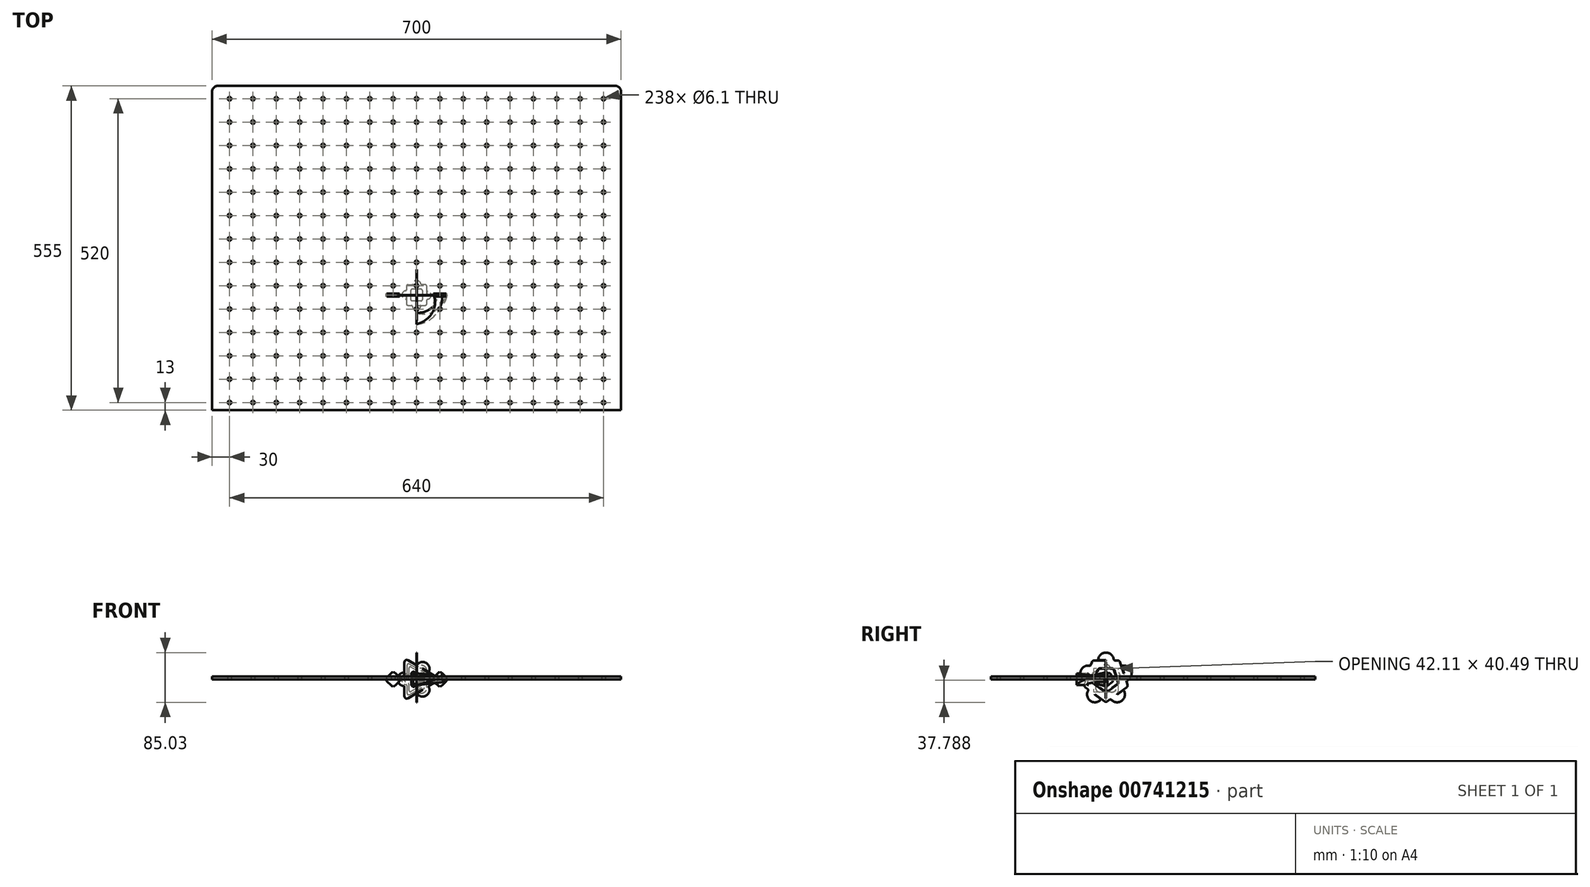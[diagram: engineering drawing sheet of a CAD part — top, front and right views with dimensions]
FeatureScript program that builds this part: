
annotation { "Feature Type Name" : "Feature", "Feature Type Description" : "" }
export const myFeature = defineFeature(function(context is Context, id is Id, definition is map)
    precondition{}
    {
        {
            var Q0;
            Q0=qCreatedBy(makeId("Top.planeOp"),FACE);
            var sketch = newSketch(context, id + "F0", { "sketchPlane" : qUnion([Q0])});
            skLineSegment(sketch, "E0.bottom", {"start": v(340, 358) * mm, "end": v(-340, 358) * mm});
            skLineSegment(sketch, "E0.top", {"start": v(340, -358) * mm, "end": v(-350, -358) * mm});
            skLineSegment(sketch, "E0.left", {"start": v(350, 348) * mm, "end": v(350, -348) * mm});
            skLineSegment(sketch, "E0.right", {"start": v(-350, 348) * mm, "end": v(-350, -358) * mm});
            skPoint(sketch, "E0.middle", {"position": v(0, 0) * mm});
            skLineSegment(sketch, "E1.0", {"start": v(324, 342) * mm, "end": v(-334, 342) * mm, "construction": true});
            skLineSegment(sketch, "E1.1", {"start": v(334, 332) * mm, "end": v(334, -342) * mm, "construction": true});
            skLineSegment(sketch, "E1.2", {"start": v(334, -342) * mm, "end": v(-334, -342) * mm, "construction": true});
            skLineSegment(sketch, "E1.3", {"start": v(-334, 342) * mm, "end": v(-334, -342) * mm, "construction": true});
            skCircle(sketch, "E2", {"center": v(-320, 336) * mm, "radius": 3.05 * mm});
            skCircle(sketch, "E3.0.1.0", {"center": v(-320, 296) * mm, "radius": 3.05 * mm});
            skCircle(sketch, "E3.1.0.0", {"center": v(-280, 336) * mm, "radius": 3.05 * mm});
            skCircle(sketch, "E3.1.1.0", {"center": v(-280, 296) * mm, "radius": 3.05 * mm});
            skCircle(sketch, "E3.2.0.0", {"center": v(-240, 336) * mm, "radius": 3.05 * mm});
            skCircle(sketch, "E3.2.1.0", {"center": v(-240, 296) * mm, "radius": 3.05 * mm});
            skCircle(sketch, "E3.3.0.0", {"center": v(-200, 336) * mm, "radius": 3.05 * mm});
            skCircle(sketch, "E3.3.1.0", {"center": v(-200, 296) * mm, "radius": 3.05 * mm});
            skCircle(sketch, "E3.4.0.0", {"center": v(-160, 336) * mm, "radius": 3.05 * mm});
            skCircle(sketch, "E3.4.1.0", {"center": v(-160, 296) * mm, "radius": 3.05 * mm});
            skCircle(sketch, "E3.5.0.0", {"center": v(-120, 336) * mm, "radius": 3.05 * mm});
            skCircle(sketch, "E3.5.1.0", {"center": v(-120, 296) * mm, "radius": 3.05 * mm});
            skCircle(sketch, "E3.6.0.0", {"center": v(-80, 336) * mm, "radius": 3.05 * mm});
            skCircle(sketch, "E3.6.1.0", {"center": v(-80, 296) * mm, "radius": 3.05 * mm});
            skCircle(sketch, "E3.7.0.0", {"center": v(-40, 336) * mm, "radius": 3.05 * mm});
            skCircle(sketch, "E3.7.1.0", {"center": v(-40, 296) * mm, "radius": 3.05 * mm});
            skCircle(sketch, "E3.8.0.0", {"center": v(0, 336) * mm, "radius": 3.05 * mm});
            skCircle(sketch, "E3.8.1.0", {"center": v(0, 296) * mm, "radius": 3.05 * mm});
            skCircle(sketch, "E3.9.0.0", {"center": v(40, 336) * mm, "radius": 3.05 * mm});
            skCircle(sketch, "E3.9.1.0", {"center": v(40, 296) * mm, "radius": 3.05 * mm});
            skCircle(sketch, "E3.10.0.0", {"center": v(80, 336) * mm, "radius": 3.05 * mm});
            skCircle(sketch, "E3.10.1.0", {"center": v(80, 296) * mm, "radius": 3.05 * mm});
            skCircle(sketch, "E3.11.0.0", {"center": v(120, 336) * mm, "radius": 3.05 * mm});
            skCircle(sketch, "E3.11.1.0", {"center": v(120, 296) * mm, "radius": 3.05 * mm});
            skCircle(sketch, "E3.12.0.0", {"center": v(160, 336) * mm, "radius": 3.05 * mm});
            skCircle(sketch, "E3.12.1.0", {"center": v(160, 296) * mm, "radius": 3.05 * mm});
            skCircle(sketch, "E3.13.0.0", {"center": v(200, 336) * mm, "radius": 3.05 * mm});
            skCircle(sketch, "E3.13.1.0", {"center": v(200, 296) * mm, "radius": 3.05 * mm});
            skLineSegment(sketch, "E3.direction1", {"start": v(-320, 336) * mm, "end": v(-280, 336) * mm, "construction": true});
            skLineSegment(sketch, "E3.direction2", {"start": v(-320, 336) * mm, "end": v(-320, 296) * mm, "construction": true});
            skCircle(sketch, "E4.0.0.2", {"center": v(-320, 256) * mm, "radius": 3.05 * mm});
            skCircle(sketch, "E4.0.0.3", {"center": v(-320, 216) * mm, "radius": 3.05 * mm});
            skCircle(sketch, "E4.0.0.4", {"center": v(-320, 176) * mm, "radius": 3.05 * mm});
            skCircle(sketch, "E4.0.0.5", {"center": v(-320, 136) * mm, "radius": 3.05 * mm});
            skCircle(sketch, "E4.0.0.6", {"center": v(-320, 96) * mm, "radius": 3.05 * mm});
            skCircle(sketch, "E4.0.0.7", {"center": v(-320, 56) * mm, "radius": 3.05 * mm});
            skCircle(sketch, "E4.0.0.8", {"center": v(-320, 16) * mm, "radius": 3.05 * mm});
            skCircle(sketch, "E4.0.0.9", {"center": v(-320, -24) * mm, "radius": 3.05 * mm});
            skCircle(sketch, "E4.0.0.10", {"center": v(-320, -64) * mm, "radius": 3.05 * mm});
            skCircle(sketch, "E4.0.0.11", {"center": v(-320, -104) * mm, "radius": 3.05 * mm});
            skCircle(sketch, "E4.0.0.12", {"center": v(-320, -144) * mm, "radius": 3.05 * mm});
            skCircle(sketch, "E4.0.0.13", {"center": v(-320, -184) * mm, "radius": 3.05 * mm});
            skCircle(sketch, "E4.0.1.2", {"center": v(-280, 256) * mm, "radius": 3.05 * mm});
            skCircle(sketch, "E4.0.1.3", {"center": v(-280, 216) * mm, "radius": 3.05 * mm});
            skCircle(sketch, "E4.0.1.4", {"center": v(-280, 176) * mm, "radius": 3.05 * mm});
            skCircle(sketch, "E4.0.1.5", {"center": v(-280, 136) * mm, "radius": 3.05 * mm});
            skCircle(sketch, "E4.0.1.6", {"center": v(-280, 96) * mm, "radius": 3.05 * mm});
            skCircle(sketch, "E4.0.1.7", {"center": v(-280, 56) * mm, "radius": 3.05 * mm});
            skCircle(sketch, "E4.0.1.8", {"center": v(-280, 16) * mm, "radius": 3.05 * mm});
            skCircle(sketch, "E4.0.1.9", {"center": v(-280, -24) * mm, "radius": 3.05 * mm});
            skCircle(sketch, "E4.0.1.10", {"center": v(-280, -64) * mm, "radius": 3.05 * mm});
            skCircle(sketch, "E4.0.1.11", {"center": v(-280, -104) * mm, "radius": 3.05 * mm});
            skCircle(sketch, "E4.0.1.12", {"center": v(-280, -144) * mm, "radius": 3.05 * mm});
            skCircle(sketch, "E4.0.1.13", {"center": v(-280, -184) * mm, "radius": 3.05 * mm});
            skCircle(sketch, "E4.0.2.2", {"center": v(-240, 256) * mm, "radius": 3.05 * mm});
            skCircle(sketch, "E4.0.2.3", {"center": v(-240, 216) * mm, "radius": 3.05 * mm});
            skCircle(sketch, "E4.0.2.4", {"center": v(-240, 176) * mm, "radius": 3.05 * mm});
            skCircle(sketch, "E4.0.2.5", {"center": v(-240, 136) * mm, "radius": 3.05 * mm});
            skCircle(sketch, "E4.0.2.6", {"center": v(-240, 96) * mm, "radius": 3.05 * mm});
            skCircle(sketch, "E4.0.2.7", {"center": v(-240, 56) * mm, "radius": 3.05 * mm});
            skCircle(sketch, "E4.0.2.8", {"center": v(-240, 16) * mm, "radius": 3.05 * mm});
            skCircle(sketch, "E4.0.2.9", {"center": v(-240, -24) * mm, "radius": 3.05 * mm});
            skCircle(sketch, "E4.0.2.10", {"center": v(-240, -64) * mm, "radius": 3.05 * mm});
            skCircle(sketch, "E4.0.2.11", {"center": v(-240, -104) * mm, "radius": 3.05 * mm});
            skCircle(sketch, "E4.0.2.12", {"center": v(-240, -144) * mm, "radius": 3.05 * mm});
            skCircle(sketch, "E4.0.2.13", {"center": v(-240, -184) * mm, "radius": 3.05 * mm});
            skCircle(sketch, "E4.0.3.2", {"center": v(-200, 256) * mm, "radius": 3.05 * mm});
            skCircle(sketch, "E4.0.3.3", {"center": v(-200, 216) * mm, "radius": 3.05 * mm});
            skCircle(sketch, "E4.0.3.4", {"center": v(-200, 176) * mm, "radius": 3.05 * mm});
            skCircle(sketch, "E4.0.3.5", {"center": v(-200, 136) * mm, "radius": 3.05 * mm});
            skCircle(sketch, "E4.0.3.6", {"center": v(-200, 96) * mm, "radius": 3.05 * mm});
            skCircle(sketch, "E4.0.3.7", {"center": v(-200, 56) * mm, "radius": 3.05 * mm});
            skCircle(sketch, "E4.0.3.8", {"center": v(-200, 16) * mm, "radius": 3.05 * mm});
            skCircle(sketch, "E4.0.3.9", {"center": v(-200, -24) * mm, "radius": 3.05 * mm});
            skCircle(sketch, "E4.0.3.10", {"center": v(-200, -64) * mm, "radius": 3.05 * mm});
            skCircle(sketch, "E4.0.3.11", {"center": v(-200, -104) * mm, "radius": 3.05 * mm});
            skCircle(sketch, "E4.0.3.12", {"center": v(-200, -144) * mm, "radius": 3.05 * mm});
            skCircle(sketch, "E4.0.3.13", {"center": v(-200, -184) * mm, "radius": 3.05 * mm});
            skCircle(sketch, "E4.0.4.2", {"center": v(-160, 256) * mm, "radius": 3.05 * mm});
            skCircle(sketch, "E4.0.4.3", {"center": v(-160, 216) * mm, "radius": 3.05 * mm});
            skCircle(sketch, "E4.0.4.4", {"center": v(-160, 176) * mm, "radius": 3.05 * mm});
            skCircle(sketch, "E4.0.4.5", {"center": v(-160, 136) * mm, "radius": 3.05 * mm});
            skCircle(sketch, "E4.0.4.6", {"center": v(-160, 96) * mm, "radius": 3.05 * mm});
            skCircle(sketch, "E4.0.4.7", {"center": v(-160, 56) * mm, "radius": 3.05 * mm});
            skCircle(sketch, "E4.0.4.8", {"center": v(-160, 16) * mm, "radius": 3.05 * mm});
            skCircle(sketch, "E4.0.4.9", {"center": v(-160, -24) * mm, "radius": 3.05 * mm});
            skCircle(sketch, "E4.0.4.10", {"center": v(-160, -64) * mm, "radius": 3.05 * mm});
            skCircle(sketch, "E4.0.4.11", {"center": v(-160, -104) * mm, "radius": 3.05 * mm});
            skCircle(sketch, "E4.0.4.12", {"center": v(-160, -144) * mm, "radius": 3.05 * mm});
            skCircle(sketch, "E4.0.4.13", {"center": v(-160, -184) * mm, "radius": 3.05 * mm});
            skCircle(sketch, "E4.0.5.2", {"center": v(-120, 256) * mm, "radius": 3.05 * mm});
            skCircle(sketch, "E4.0.5.3", {"center": v(-120, 216) * mm, "radius": 3.05 * mm});
            skCircle(sketch, "E4.0.5.4", {"center": v(-120, 176) * mm, "radius": 3.05 * mm});
            skCircle(sketch, "E4.0.5.5", {"center": v(-120, 136) * mm, "radius": 3.05 * mm});
            skCircle(sketch, "E4.0.5.6", {"center": v(-120, 96) * mm, "radius": 3.05 * mm});
            skCircle(sketch, "E4.0.5.7", {"center": v(-120, 56) * mm, "radius": 3.05 * mm});
            skCircle(sketch, "E4.0.5.8", {"center": v(-120, 16) * mm, "radius": 3.05 * mm});
            skCircle(sketch, "E4.0.5.9", {"center": v(-120, -24) * mm, "radius": 3.05 * mm});
            skCircle(sketch, "E4.0.5.10", {"center": v(-120, -64) * mm, "radius": 3.05 * mm});
            skCircle(sketch, "E4.0.5.11", {"center": v(-120, -104) * mm, "radius": 3.05 * mm});
            skCircle(sketch, "E4.0.5.12", {"center": v(-120, -144) * mm, "radius": 3.05 * mm});
            skCircle(sketch, "E4.0.5.13", {"center": v(-120, -184) * mm, "radius": 3.05 * mm});
            skCircle(sketch, "E4.0.6.2", {"center": v(-80, 256) * mm, "radius": 3.05 * mm});
            skCircle(sketch, "E4.0.6.3", {"center": v(-80, 216) * mm, "radius": 3.05 * mm});
            skCircle(sketch, "E4.0.6.4", {"center": v(-80, 176) * mm, "radius": 3.05 * mm});
            skCircle(sketch, "E4.0.6.5", {"center": v(-80, 136) * mm, "radius": 3.05 * mm});
            skCircle(sketch, "E4.0.6.6", {"center": v(-80, 96) * mm, "radius": 3.05 * mm});
            skCircle(sketch, "E4.0.6.7", {"center": v(-80, 56) * mm, "radius": 3.05 * mm});
            skCircle(sketch, "E4.0.6.8", {"center": v(-80, 16) * mm, "radius": 3.05 * mm});
            skCircle(sketch, "E4.0.6.9", {"center": v(-80, -24) * mm, "radius": 3.05 * mm});
            skCircle(sketch, "E4.0.6.10", {"center": v(-80, -64) * mm, "radius": 3.05 * mm});
            skCircle(sketch, "E4.0.6.11", {"center": v(-80, -104) * mm, "radius": 3.05 * mm});
            skCircle(sketch, "E4.0.6.12", {"center": v(-80, -144) * mm, "radius": 3.05 * mm});
            skCircle(sketch, "E4.0.6.13", {"center": v(-80, -184) * mm, "radius": 3.05 * mm});
            skCircle(sketch, "E4.0.7.2", {"center": v(-40, 256) * mm, "radius": 3.05 * mm});
            skCircle(sketch, "E4.0.7.3", {"center": v(-40, 216) * mm, "radius": 3.05 * mm});
            skCircle(sketch, "E4.0.7.4", {"center": v(-40, 176) * mm, "radius": 3.05 * mm});
            skCircle(sketch, "E4.0.7.5", {"center": v(-40, 136) * mm, "radius": 3.05 * mm});
            skCircle(sketch, "E4.0.7.6", {"center": v(-40, 96) * mm, "radius": 3.05 * mm});
            skCircle(sketch, "E4.0.7.7", {"center": v(-40, 56) * mm, "radius": 3.05 * mm});
            skCircle(sketch, "E4.0.7.8", {"center": v(-40, 16) * mm, "radius": 3.05 * mm});
            skCircle(sketch, "E4.0.7.9", {"center": v(-40, -24) * mm, "radius": 3.05 * mm});
            skCircle(sketch, "E4.0.7.10", {"center": v(-40, -64) * mm, "radius": 3.05 * mm});
            skCircle(sketch, "E4.0.7.11", {"center": v(-40, -104) * mm, "radius": 3.05 * mm});
            skCircle(sketch, "E4.0.7.12", {"center": v(-40, -144) * mm, "radius": 3.05 * mm});
            skCircle(sketch, "E4.0.7.13", {"center": v(-40, -184) * mm, "radius": 3.05 * mm});
            skCircle(sketch, "E4.0.8.2", {"center": v(0, 256) * mm, "radius": 3.05 * mm});
            skCircle(sketch, "E4.0.8.3", {"center": v(0, 216) * mm, "radius": 3.05 * mm});
            skCircle(sketch, "E4.0.8.4", {"center": v(0, 176) * mm, "radius": 3.05 * mm});
            skCircle(sketch, "E4.0.8.5", {"center": v(0, 136) * mm, "radius": 3.05 * mm});
            skCircle(sketch, "E4.0.8.6", {"center": v(0, 96) * mm, "radius": 3.05 * mm});
            skCircle(sketch, "E4.0.8.7", {"center": v(0, 56) * mm, "radius": 3.05 * mm});
            skCircle(sketch, "E4.0.8.8", {"center": v(0, 16) * mm, "radius": 3.05 * mm});
            skCircle(sketch, "E4.0.8.9", {"center": v(0, -24) * mm, "radius": 3.05 * mm});
            skCircle(sketch, "E4.0.8.10", {"center": v(0, -64) * mm, "radius": 3.05 * mm});
            skCircle(sketch, "E4.0.8.11", {"center": v(0, -104) * mm, "radius": 3.05 * mm});
            skCircle(sketch, "E4.0.8.12", {"center": v(0, -144) * mm, "radius": 3.05 * mm});
            skCircle(sketch, "E4.0.8.13", {"center": v(0, -184) * mm, "radius": 3.05 * mm});
            skCircle(sketch, "E4.0.9.2", {"center": v(40, 256) * mm, "radius": 3.05 * mm});
            skCircle(sketch, "E4.0.9.3", {"center": v(40, 216) * mm, "radius": 3.05 * mm});
            skCircle(sketch, "E4.0.9.4", {"center": v(40, 176) * mm, "radius": 3.05 * mm});
            skCircle(sketch, "E4.0.9.5", {"center": v(40, 136) * mm, "radius": 3.05 * mm});
            skCircle(sketch, "E4.0.9.6", {"center": v(40, 96) * mm, "radius": 3.05 * mm});
            skCircle(sketch, "E4.0.9.7", {"center": v(40, 56) * mm, "radius": 3.05 * mm});
            skCircle(sketch, "E4.0.9.8", {"center": v(40, 16) * mm, "radius": 3.05 * mm});
            skCircle(sketch, "E4.0.9.9", {"center": v(40, -24) * mm, "radius": 3.05 * mm});
            skCircle(sketch, "E4.0.9.10", {"center": v(40, -64) * mm, "radius": 3.05 * mm});
            skCircle(sketch, "E4.0.9.11", {"center": v(40, -104) * mm, "radius": 3.05 * mm});
            skCircle(sketch, "E4.0.9.12", {"center": v(40, -144) * mm, "radius": 3.05 * mm});
            skCircle(sketch, "E4.0.9.13", {"center": v(40, -184) * mm, "radius": 3.05 * mm});
            skCircle(sketch, "E4.0.10.2", {"center": v(80, 256) * mm, "radius": 3.05 * mm});
            skCircle(sketch, "E4.0.10.3", {"center": v(80, 216) * mm, "radius": 3.05 * mm});
            skCircle(sketch, "E4.0.10.4", {"center": v(80, 176) * mm, "radius": 3.05 * mm});
            skCircle(sketch, "E4.0.10.5", {"center": v(80, 136) * mm, "radius": 3.05 * mm});
            skCircle(sketch, "E4.0.10.6", {"center": v(80, 96) * mm, "radius": 3.05 * mm});
            skCircle(sketch, "E4.0.10.7", {"center": v(80, 56) * mm, "radius": 3.05 * mm});
            skCircle(sketch, "E4.0.10.8", {"center": v(80, 16) * mm, "radius": 3.05 * mm});
            skCircle(sketch, "E4.0.10.9", {"center": v(80, -24) * mm, "radius": 3.05 * mm});
            skCircle(sketch, "E4.0.10.10", {"center": v(80, -64) * mm, "radius": 3.05 * mm});
            skCircle(sketch, "E4.0.10.11", {"center": v(80, -104) * mm, "radius": 3.05 * mm});
            skCircle(sketch, "E4.0.10.12", {"center": v(80, -144) * mm, "radius": 3.05 * mm});
            skCircle(sketch, "E4.0.10.13", {"center": v(80, -184) * mm, "radius": 3.05 * mm});
            skCircle(sketch, "E4.0.11.2", {"center": v(120, 256) * mm, "radius": 3.05 * mm});
            skCircle(sketch, "E4.0.11.3", {"center": v(120, 216) * mm, "radius": 3.05 * mm});
            skCircle(sketch, "E4.0.11.4", {"center": v(120, 176) * mm, "radius": 3.05 * mm});
            skCircle(sketch, "E4.0.11.5", {"center": v(120, 136) * mm, "radius": 3.05 * mm});
            skCircle(sketch, "E4.0.11.6", {"center": v(120, 96) * mm, "radius": 3.05 * mm});
            skCircle(sketch, "E4.0.11.7", {"center": v(120, 56) * mm, "radius": 3.05 * mm});
            skCircle(sketch, "E4.0.11.8", {"center": v(120, 16) * mm, "radius": 3.05 * mm});
            skCircle(sketch, "E4.0.11.9", {"center": v(120, -24) * mm, "radius": 3.05 * mm});
            skCircle(sketch, "E4.0.11.10", {"center": v(120, -64) * mm, "radius": 3.05 * mm});
            skCircle(sketch, "E4.0.11.11", {"center": v(120, -104) * mm, "radius": 3.05 * mm});
            skCircle(sketch, "E4.0.11.12", {"center": v(120, -144) * mm, "radius": 3.05 * mm});
            skCircle(sketch, "E4.0.11.13", {"center": v(120, -184) * mm, "radius": 3.05 * mm});
            skCircle(sketch, "E4.0.12.2", {"center": v(160, 256) * mm, "radius": 3.05 * mm});
            skCircle(sketch, "E4.0.12.3", {"center": v(160, 216) * mm, "radius": 3.05 * mm});
            skCircle(sketch, "E4.0.12.4", {"center": v(160, 176) * mm, "radius": 3.05 * mm});
            skCircle(sketch, "E4.0.12.5", {"center": v(160, 136) * mm, "radius": 3.05 * mm});
            skCircle(sketch, "E4.0.12.6", {"center": v(160, 96) * mm, "radius": 3.05 * mm});
            skCircle(sketch, "E4.0.12.7", {"center": v(160, 56) * mm, "radius": 3.05 * mm});
            skCircle(sketch, "E4.0.12.8", {"center": v(160, 16) * mm, "radius": 3.05 * mm});
            skCircle(sketch, "E4.0.12.9", {"center": v(160, -24) * mm, "radius": 3.05 * mm});
            skCircle(sketch, "E4.0.12.10", {"center": v(160, -64) * mm, "radius": 3.05 * mm});
            skCircle(sketch, "E4.0.12.11", {"center": v(160, -104) * mm, "radius": 3.05 * mm});
            skCircle(sketch, "E4.0.12.12", {"center": v(160, -144) * mm, "radius": 3.05 * mm});
            skCircle(sketch, "E4.0.12.13", {"center": v(160, -184) * mm, "radius": 3.05 * mm});
            skCircle(sketch, "E4.0.13.2", {"center": v(200, 256) * mm, "radius": 3.05 * mm});
            skCircle(sketch, "E4.0.13.3", {"center": v(200, 216) * mm, "radius": 3.05 * mm});
            skCircle(sketch, "E4.0.13.4", {"center": v(200, 176) * mm, "radius": 3.05 * mm});
            skCircle(sketch, "E4.0.13.5", {"center": v(200, 136) * mm, "radius": 3.05 * mm});
            skCircle(sketch, "E4.0.13.6", {"center": v(200, 96) * mm, "radius": 3.05 * mm});
            skCircle(sketch, "E4.0.13.7", {"center": v(200, 56) * mm, "radius": 3.05 * mm});
            skCircle(sketch, "E4.0.13.8", {"center": v(200, 16) * mm, "radius": 3.05 * mm});
            skCircle(sketch, "E4.0.13.9", {"center": v(200, -24) * mm, "radius": 3.05 * mm});
            skCircle(sketch, "E4.0.13.10", {"center": v(200, -64) * mm, "radius": 3.05 * mm});
            skCircle(sketch, "E4.0.13.11", {"center": v(200, -104) * mm, "radius": 3.05 * mm});
            skCircle(sketch, "E4.0.13.12", {"center": v(200, -144) * mm, "radius": 3.05 * mm});
            skCircle(sketch, "E4.0.13.13", {"center": v(200, -184) * mm, "radius": 3.05 * mm});
            skLineSegment(sketch, "E5", {"start": v(0, 358) * mm, "end": v(0, -358) * mm});
            skCircle(sketch, "E6.0.14.0", {"center": v(240, 336) * mm, "radius": 3.05 * mm});
            skCircle(sketch, "E6.0.14.1", {"center": v(240, 296) * mm, "radius": 3.05 * mm});
            skCircle(sketch, "E6.0.14.2", {"center": v(240, 256) * mm, "radius": 3.05 * mm});
            skCircle(sketch, "E6.0.14.3", {"center": v(240, 216) * mm, "radius": 3.05 * mm});
            skCircle(sketch, "E6.0.14.4", {"center": v(240, 176) * mm, "radius": 3.05 * mm});
            skCircle(sketch, "E6.0.14.5", {"center": v(240, 136) * mm, "radius": 3.05 * mm});
            skCircle(sketch, "E6.0.14.6", {"center": v(240, 96) * mm, "radius": 3.05 * mm});
            skCircle(sketch, "E6.0.14.7", {"center": v(240, 56) * mm, "radius": 3.05 * mm});
            skCircle(sketch, "E6.0.14.8", {"center": v(240, 16) * mm, "radius": 3.05 * mm});
            skCircle(sketch, "E6.0.14.9", {"center": v(240, -24) * mm, "radius": 3.05 * mm});
            skCircle(sketch, "E6.0.14.10", {"center": v(240, -64) * mm, "radius": 3.05 * mm});
            skCircle(sketch, "E6.0.14.11", {"center": v(240, -104) * mm, "radius": 3.05 * mm});
            skCircle(sketch, "E6.0.14.12", {"center": v(240, -144) * mm, "radius": 3.05 * mm});
            skCircle(sketch, "E6.0.14.13", {"center": v(240, -184) * mm, "radius": 3.05 * mm});
            skCircle(sketch, "E6.0.15.0", {"center": v(280, 336) * mm, "radius": 3.05 * mm});
            skCircle(sketch, "E6.0.15.1", {"center": v(280, 296) * mm, "radius": 3.05 * mm});
            skCircle(sketch, "E6.0.15.2", {"center": v(280, 256) * mm, "radius": 3.05 * mm});
            skCircle(sketch, "E6.0.15.3", {"center": v(280, 216) * mm, "radius": 3.05 * mm});
            skCircle(sketch, "E6.0.15.4", {"center": v(280, 176) * mm, "radius": 3.05 * mm});
            skCircle(sketch, "E6.0.15.5", {"center": v(280, 136) * mm, "radius": 3.05 * mm});
            skCircle(sketch, "E6.0.15.6", {"center": v(280, 96) * mm, "radius": 3.05 * mm});
            skCircle(sketch, "E6.0.15.7", {"center": v(280, 56) * mm, "radius": 3.05 * mm});
            skCircle(sketch, "E6.0.15.8", {"center": v(280, 16) * mm, "radius": 3.05 * mm});
            skCircle(sketch, "E6.0.15.9", {"center": v(280, -24) * mm, "radius": 3.05 * mm});
            skCircle(sketch, "E6.0.15.10", {"center": v(280, -64) * mm, "radius": 3.05 * mm});
            skCircle(sketch, "E6.0.15.11", {"center": v(280, -104) * mm, "radius": 3.05 * mm});
            skCircle(sketch, "E6.0.15.12", {"center": v(280, -144) * mm, "radius": 3.05 * mm});
            skCircle(sketch, "E6.0.15.13", {"center": v(280, -184) * mm, "radius": 3.05 * mm});
            skCircle(sketch, "E6.0.16.0", {"center": v(320, 336) * mm, "radius": 3.05 * mm});
            skCircle(sketch, "E6.0.16.1", {"center": v(320, 296) * mm, "radius": 3.05 * mm});
            skCircle(sketch, "E6.0.16.2", {"center": v(320, 256) * mm, "radius": 3.05 * mm});
            skCircle(sketch, "E6.0.16.3", {"center": v(320, 216) * mm, "radius": 3.05 * mm});
            skCircle(sketch, "E6.0.16.4", {"center": v(320, 176) * mm, "radius": 3.05 * mm});
            skCircle(sketch, "E6.0.16.5", {"center": v(320, 136) * mm, "radius": 3.05 * mm});
            skCircle(sketch, "E6.0.16.6", {"center": v(320, 96) * mm, "radius": 3.05 * mm});
            skCircle(sketch, "E6.0.16.7", {"center": v(320, 56) * mm, "radius": 3.05 * mm});
            skCircle(sketch, "E6.0.16.8", {"center": v(320, 16) * mm, "radius": 3.05 * mm});
            skCircle(sketch, "E6.0.16.9", {"center": v(320, -24) * mm, "radius": 3.05 * mm});
            skCircle(sketch, "E6.0.16.10", {"center": v(320, -64) * mm, "radius": 3.05 * mm});
            skCircle(sketch, "E6.0.16.11", {"center": v(320, -104) * mm, "radius": 3.05 * mm});
            skCircle(sketch, "E6.0.16.12", {"center": v(320, -144) * mm, "radius": 3.05 * mm});
            skCircle(sketch, "E6.0.16.13", {"center": v(320, -184) * mm, "radius": 3.05 * mm});
            skCircle(sketch, "E7.0.0.14", {"center": v(-320, -224) * mm, "radius": 3.05 * mm});
            skCircle(sketch, "E7.0.0.15", {"center": v(-320, -264) * mm, "radius": 3.05 * mm});
            skCircle(sketch, "E7.0.0.16", {"center": v(-320, -304) * mm, "radius": 3.05 * mm});
            skCircle(sketch, "E7.0.1.14", {"center": v(-280, -224) * mm, "radius": 3.05 * mm});
            skCircle(sketch, "E7.0.1.15", {"center": v(-280, -264) * mm, "radius": 3.05 * mm});
            skCircle(sketch, "E7.0.1.16", {"center": v(-280, -304) * mm, "radius": 3.05 * mm});
            skCircle(sketch, "E7.0.2.14", {"center": v(-240, -224) * mm, "radius": 3.05 * mm});
            skCircle(sketch, "E7.0.2.15", {"center": v(-240, -264) * mm, "radius": 3.05 * mm});
            skCircle(sketch, "E7.0.2.16", {"center": v(-240, -304) * mm, "radius": 3.05 * mm});
            skCircle(sketch, "E7.0.3.14", {"center": v(-200, -224) * mm, "radius": 3.05 * mm});
            skCircle(sketch, "E7.0.3.15", {"center": v(-200, -264) * mm, "radius": 3.05 * mm});
            skCircle(sketch, "E7.0.3.16", {"center": v(-200, -304) * mm, "radius": 3.05 * mm});
            skCircle(sketch, "E7.0.4.14", {"center": v(-160, -224) * mm, "radius": 3.05 * mm});
            skCircle(sketch, "E7.0.4.15", {"center": v(-160, -264) * mm, "radius": 3.05 * mm});
            skCircle(sketch, "E7.0.4.16", {"center": v(-160, -304) * mm, "radius": 3.05 * mm});
            skCircle(sketch, "E7.0.5.14", {"center": v(-120, -224) * mm, "radius": 3.05 * mm});
            skCircle(sketch, "E7.0.5.15", {"center": v(-120, -264) * mm, "radius": 3.05 * mm});
            skCircle(sketch, "E7.0.5.16", {"center": v(-120, -304) * mm, "radius": 3.05 * mm});
            skCircle(sketch, "E7.0.6.14", {"center": v(-80, -224) * mm, "radius": 3.05 * mm});
            skCircle(sketch, "E7.0.6.15", {"center": v(-80, -264) * mm, "radius": 3.05 * mm});
            skCircle(sketch, "E7.0.6.16", {"center": v(-80, -304) * mm, "radius": 3.05 * mm});
            skCircle(sketch, "E7.0.7.14", {"center": v(-40, -224) * mm, "radius": 3.05 * mm});
            skCircle(sketch, "E7.0.7.15", {"center": v(-40, -264) * mm, "radius": 3.05 * mm});
            skCircle(sketch, "E7.0.7.16", {"center": v(-40, -304) * mm, "radius": 3.05 * mm});
            skCircle(sketch, "E7.0.8.14", {"center": v(0, -224) * mm, "radius": 3.05 * mm});
            skCircle(sketch, "E7.0.8.15", {"center": v(0, -264) * mm, "radius": 3.05 * mm});
            skCircle(sketch, "E7.0.8.16", {"center": v(0, -304) * mm, "radius": 3.05 * mm});
            skCircle(sketch, "E7.0.9.14", {"center": v(40, -224) * mm, "radius": 3.05 * mm});
            skCircle(sketch, "E7.0.9.15", {"center": v(40, -264) * mm, "radius": 3.05 * mm});
            skCircle(sketch, "E7.0.9.16", {"center": v(40, -304) * mm, "radius": 3.05 * mm});
            skCircle(sketch, "E7.0.10.14", {"center": v(80, -224) * mm, "radius": 3.05 * mm});
            skCircle(sketch, "E7.0.10.15", {"center": v(80, -264) * mm, "radius": 3.05 * mm});
            skCircle(sketch, "E7.0.10.16", {"center": v(80, -304) * mm, "radius": 3.05 * mm});
            skCircle(sketch, "E7.0.11.14", {"center": v(120, -224) * mm, "radius": 3.05 * mm});
            skCircle(sketch, "E7.0.11.15", {"center": v(120, -264) * mm, "radius": 3.05 * mm});
            skCircle(sketch, "E7.0.11.16", {"center": v(120, -304) * mm, "radius": 3.05 * mm});
            skCircle(sketch, "E7.0.12.14", {"center": v(160, -224) * mm, "radius": 3.05 * mm});
            skCircle(sketch, "E7.0.12.15", {"center": v(160, -264) * mm, "radius": 3.05 * mm});
            skCircle(sketch, "E7.0.12.16", {"center": v(160, -304) * mm, "radius": 3.05 * mm});
            skCircle(sketch, "E7.0.13.14", {"center": v(200, -224) * mm, "radius": 3.05 * mm});
            skCircle(sketch, "E7.0.13.15", {"center": v(200, -264) * mm, "radius": 3.05 * mm});
            skCircle(sketch, "E7.0.13.16", {"center": v(200, -304) * mm, "radius": 3.05 * mm});
            skCircle(sketch, "E7.0.14.14", {"center": v(240, -224) * mm, "radius": 3.05 * mm});
            skCircle(sketch, "E7.0.14.15", {"center": v(240, -264) * mm, "radius": 3.05 * mm});
            skCircle(sketch, "E7.0.14.16", {"center": v(240, -304) * mm, "radius": 3.05 * mm});
            skCircle(sketch, "E7.0.15.14", {"center": v(280, -224) * mm, "radius": 3.05 * mm});
            skCircle(sketch, "E7.0.15.15", {"center": v(280, -264) * mm, "radius": 3.05 * mm});
            skCircle(sketch, "E7.0.15.16", {"center": v(280, -304) * mm, "radius": 3.05 * mm});
            skCircle(sketch, "E7.0.16.14", {"center": v(320, -224) * mm, "radius": 3.05 * mm});
            skCircle(sketch, "E7.0.16.15", {"center": v(320, -264) * mm, "radius": 3.05 * mm});
            skCircle(sketch, "E7.0.16.16", {"center": v(320, -304) * mm, "radius": 3.05 * mm});
            skPoint(sketch, "E8.visualSharp", {"position": v(334, 342) * mm});
            skPoint(sketch, "E9.visualSharp", {"position": v(350, -358) * mm});
            skArc(sketch, "E9.filletArc", {"start": v(340, -358) * mm, "mid": v(347.07, -355.07) * mm, "end": v(350, -348) * mm});
            skPoint(sketch, "E10.visualSharp", {"position": v(350, 358) * mm});
            skArc(sketch, "E10.filletArc", {"start": v(350, 348) * mm, "mid": v(347.07, 355.07) * mm, "end": v(340, 358) * mm});
            skLineSegment(sketch, "E11", {"start": v(-350, -197) * mm, "end": v(350, -197) * mm});
            skPoint(sketch, "E12.visualSharp", {"position": v(-350, 358) * mm});
            skArc(sketch, "E12.filletArc", {"start": v(-340, 358) * mm, "mid": v(-347.07, 355.07) * mm, "end": v(-350, 348) * mm});
            skSolve(sketch);
        }
        {
            var Q0;
            Q0=makeQuery(id+"F0.imprint","IMPRINT",FACE,{"disambiguationData":[TD([[makeQuery(id+"F0.imprint","IMPRINT",EDGE,{"derivedFrom":sQuery(id+"F0.wireOp",EDGE,"E2")}),-1.0]])]});
            var Q1;
            Q1=makeQuery(id+"F0.imprint","IMPRINT",FACE,{"disambiguationData":[TD([[makeQuery(id+"F0.imprint","IMPRINT",EDGE,{"derivedFrom":sQuery(id+"F0.wireOp",EDGE,"E3.9.0.0")}),-1.0]])]});
            extrude(context, id + "F1", {"entities" : qUnion([Q0, Q1]), "depth" : 5 * mm, "offsetDistance" : 25 * mm});
        }
        {
            var Q0;
            Q0=qCreatedBy(makeId("Top.planeOp"),FACE);
            var sketch = newSketch(context, id + "F2", { "sketchPlane" : qUnion([Q0])});
            skLineSegment(sketch, "E13.bottom", {"start": v(15, 20) * mm, "end": v(-15, 20) * mm});
            skLineSegment(sketch, "E13.top", {"start": v(15, -20) * mm, "end": v(-15, -20) * mm});
            skLineSegment(sketch, "E13.left", {"start": v(20, 15) * mm, "end": v(20, -15) * mm});
            skLineSegment(sketch, "E13.right", {"start": v(-20, 15) * mm, "end": v(-20, -15) * mm});
            skPoint(sketch, "E13.middle", {"position": v(0, 0) * mm});
            skLineSegment(sketch, "E14.2", {"start": v(-35, 30) * mm, "end": v(-35, 15) * mm});
            skArc(sketch, "E15", {"start": v(-35, 15) * mm, "mid": v(-49.9, 1.74) * mm, "end": v(-38.46, -14.6) * mm});
            skLineSegment(sketch, "E16.trimOffspring", {"start": v(-35, -15) * mm, "end": v(-35, -30) * mm});
            skLineSegment(sketch, "E17.left", {"start": v(-35, 0) * mm, "end": v(-35, -15) * mm});
            skLineSegment(sketch, "E17.right", {"start": v(-36, 0) * mm, "end": v(-36, -12.65) * mm});
            skPoint(sketch, "E18.visualSharp", {"position": v(-35, 35) * mm});
            skArc(sketch, "E18.filletArc", {"start": v(-30, 35) * mm, "mid": v(-33.54, 33.54) * mm, "end": v(-35, 30) * mm});
            skPoint(sketch, "E19.visualSharp", {"position": v(-20, 20) * mm});
            skArc(sketch, "E19.filletArc", {"start": v(-15, 20) * mm, "mid": v(-18.54, 18.54) * mm, "end": v(-20, 15) * mm});
            skPoint(sketch, "E20.visualSharp", {"position": v(20, 20) * mm});
            skArc(sketch, "E20.filletArc", {"start": v(20, 15) * mm, "mid": v(18.54, 18.54) * mm, "end": v(15, 20) * mm});
            skPoint(sketch, "E21.visualSharp", {"position": v(35, 35) * mm});
            skArc(sketch, "E21.filletArc", {"start": v(35, 30) * mm, "mid": v(33.54, 33.54) * mm, "end": v(30, 35) * mm});
            skPoint(sketch, "E22.visualSharp", {"position": v(20, -20) * mm});
            skArc(sketch, "E22.filletArc", {"start": v(15, -20) * mm, "mid": v(18.54, -18.54) * mm, "end": v(20, -15) * mm});
            skPoint(sketch, "E23.visualSharp", {"position": v(-20, -20) * mm});
            skArc(sketch, "E23.filletArc", {"start": v(-20, -15) * mm, "mid": v(-18.54, -18.54) * mm, "end": v(-15, -20) * mm});
            skPoint(sketch, "E24.visualSharp", {"position": v(-35, -35) * mm});
            skArc(sketch, "E24.filletArc", {"start": v(-35, -30) * mm, "mid": v(-33.54, -33.54) * mm, "end": v(-30, -35) * mm});
            skPoint(sketch, "E25.visualSharp", {"position": v(35, -35) * mm});
            skArc(sketch, "E25.filletArc", {"start": v(30, -35) * mm, "mid": v(33.54, -33.54) * mm, "end": v(35, -30) * mm});
            skLineSegment(sketch, "E26.1.0", {"start": v(-30, -35) * mm, "end": v(-15, -35) * mm});
            skArc(sketch, "E26.1.1", {"start": v(-15, -35) * mm, "mid": v(-1.74, -49.9) * mm, "end": v(14.6, -38.46) * mm});
            skLineSegment(sketch, "E26.1.2", {"start": v(0, -36) * mm, "end": v(12.65, -36) * mm});
            skLineSegment(sketch, "E26.1.4", {"start": v(0, -35) * mm, "end": v(0, -36) * mm});
            skLineSegment(sketch, "E26.2.0", {"start": v(35, -30) * mm, "end": v(35, -15) * mm});
            skArc(sketch, "E26.2.1", {"start": v(35, -15) * mm, "mid": v(49.9, -1.74) * mm, "end": v(38.46, 14.6) * mm});
            skLineSegment(sketch, "E26.2.2", {"start": v(36, 0) * mm, "end": v(36, 12.65) * mm});
            skLineSegment(sketch, "E26.2.3", {"start": v(35, 0) * mm, "end": v(35, 15) * mm});
            skLineSegment(sketch, "E26.2.4", {"start": v(35, 0) * mm, "end": v(36, 0) * mm});
            skLineSegment(sketch, "E26.2.5", {"start": v(35, 15) * mm, "end": v(35, 30) * mm});
            skLineSegment(sketch, "E26.3.0", {"start": v(30, 35) * mm, "end": v(15, 35) * mm});
            skArc(sketch, "E26.3.1", {"start": v(15, 35) * mm, "mid": v(1.74, 49.9) * mm, "end": v(-14.6, 38.46) * mm});
            skLineSegment(sketch, "E26.3.2", {"start": v(0, 36) * mm, "end": v(-12.65, 36) * mm});
            skLineSegment(sketch, "E26.3.4", {"start": v(0, 35) * mm, "end": v(0, 36) * mm});
            skLineSegment(sketch, "E27", {"start": v(-30, 35) * mm, "end": v(0, 35) * mm});
            skLineSegment(sketch, "E28", {"start": v(0, -35) * mm, "end": v(30, -35) * mm});
            skPoint(sketch, "E29.visualSharp", {"position": v(-14.97, 36) * mm});
            skArc(sketch, "E29.filletArc", {"start": v(-14.6, 38.46) * mm, "mid": v(-14.22, 36.76) * mm, "end": v(-12.65, 36) * mm});
            skPoint(sketch, "E30.visualSharp", {"position": v(36, 14.97) * mm});
            skArc(sketch, "E30.filletArc", {"start": v(38.46, 14.6) * mm, "mid": v(36.76, 14.22) * mm, "end": v(36, 12.65) * mm});
            skPoint(sketch, "E31.visualSharp", {"position": v(14.97, -36) * mm});
            skArc(sketch, "E31.filletArc", {"start": v(14.6, -38.46) * mm, "mid": v(14.22, -36.76) * mm, "end": v(12.65, -36) * mm});
            skPoint(sketch, "E32.visualSharp", {"position": v(-36, -14.97) * mm});
            skArc(sketch, "E32.filletArc", {"start": v(-38.46, -14.6) * mm, "mid": v(-36.76, -14.22) * mm, "end": v(-36, -12.65) * mm});
            skLineSegment(sketch, "E33", {"start": v(-36, 0) * mm, "end": v(-35, 0) * mm});
            skSolve(sketch);
        }
        {
            var Q0;
            Q0=makeQuery(id+"F2.imprint","IMPRINT",FACE,{"disambiguationData":[TD([[makeQuery(id+"F2.imprint","IMPRINT",EDGE,{"derivedFrom":sQuery(id+"F2.wireOp",EDGE,"E13.bottom")}),-1.0]])]});
            extrude(context, id + "F3", {"entities" : qUnion([Q0]), "depth" : 0.5 * mm, "offsetDistance" : 25 * mm});
        }
        {
            var Q0;
            Q0=qCreatedBy(makeId("Front.planeOp"),FACE);
            var sketch = newSketch(context, id + "F4", { "sketchPlane" : qUnion([Q0])});
            skLineSegment(sketch, "E34.0", {"start": v(-11.55, -11.34) * mm, "end": v(-11.55, 11.34) * mm});
            skLineSegment(sketch, "E34.1", {"start": v(-4.05, 15.67) * mm, "end": v(15.6, 4.33) * mm});
            skLineSegment(sketch, "E34.2", {"start": v(15.6, -4.33) * mm, "end": v(-4.05, -15.67) * mm});
            skPoint(sketch, "E34.0.midPoint", {"position": v(-11.55, 0) * mm});
            skPoint(sketch, "E35.visualSharp", {"position": v(-26.55, 45.98) * mm});
            skArc(sketch, "E35.filletArc", {"start": v(-19.05, 41.65) * mm, "mid": v(-24.05, 41.65) * mm, "end": v(-26.55, 37.32) * mm});
            skPoint(sketch, "E36.visualSharp", {"position": v(-11.55, 20) * mm});
            skArc(sketch, "E36.filletArc", {"start": v(-4.05, 15.67) * mm, "mid": v(-9.05, 15.67) * mm, "end": v(-11.55, 11.34) * mm});
            skPoint(sketch, "E37.visualSharp", {"position": v(-11.55, -20) * mm});
            skArc(sketch, "E37.filletArc", {"start": v(-11.55, -11.34) * mm, "mid": v(-9.05, -15.67) * mm, "end": v(-4.05, -15.67) * mm});
            skPoint(sketch, "E38.visualSharp", {"position": v(-26.55, -45.98) * mm});
            skArc(sketch, "E38.filletArc", {"start": v(-26.55, -37.32) * mm, "mid": v(-24.05, -41.65) * mm, "end": v(-19.05, -41.65) * mm});
            skPoint(sketch, "E39.visualSharp", {"position": v(23.1, 0) * mm});
            skArc(sketch, "E39.filletArc", {"start": v(15.6, -4.33) * mm, "mid": v(18.1, 0) * mm, "end": v(15.6, 4.33) * mm});
            skPoint(sketch, "E40.visualSharp", {"position": v(53.1, 0) * mm});
            skArc(sketch, "E40.filletArc", {"start": v(45.6, -4.33) * mm, "mid": v(48.1, 0) * mm, "end": v(45.6, 4.33) * mm});
            skArc(sketch, "E41", {"start": v(-27.05, 15) * mm, "mid": v(-41.54, -0.25) * mm, "end": v(-26.55, -15) * mm});
            skLineSegment(sketch, "E42.bottom", {"start": v(-26.55, 0) * mm, "end": v(-27.05, 0) * mm});
            skLineSegment(sketch, "E42.right", {"start": v(-27.05, 0) * mm, "end": v(-27.05, 15) * mm});
            skLineSegment(sketch, "E43", {"start": v(-26.55, 37.32) * mm, "end": v(-26.55, 0) * mm});
            skLineSegment(sketch, "E44", {"start": v(-26.55, -15) * mm, "end": v(-26.55, -37.32) * mm});
            skLineSegment(sketch, "E45.1.0", {"start": v(26.26, -15.5) * mm, "end": v(45.6, -4.33) * mm});
            skLineSegment(sketch, "E45.1.1", {"start": v(-19.05, -41.65) * mm, "end": v(13.27, -23) * mm});
            skArc(sketch, "E45.1.2", {"start": v(0.54, -30.92) * mm, "mid": v(20.99, -35.85) * mm, "end": v(26.26, -15.5) * mm});
            skLineSegment(sketch, "E45.1.3", {"start": v(13.52, -23.42) * mm, "end": v(0.54, -30.92) * mm});
            skLineSegment(sketch, "E45.1.4", {"start": v(13.27, -23) * mm, "end": v(13.52, -23.42) * mm});
            skLineSegment(sketch, "E45.2.0", {"start": v(0.28, 30.5) * mm, "end": v(-19.05, 41.65) * mm});
            skLineSegment(sketch, "E45.2.1", {"start": v(45.6, 4.33) * mm, "end": v(13.27, 23) * mm});
            skArc(sketch, "E45.2.2", {"start": v(26.5, 15.93) * mm, "mid": v(20.56, 36.1) * mm, "end": v(0.28, 30.5) * mm});
            skLineSegment(sketch, "E45.2.3", {"start": v(13.52, 23.42) * mm, "end": v(26.5, 15.93) * mm});
            skLineSegment(sketch, "E45.2.4", {"start": v(13.27, 23) * mm, "end": v(13.52, 23.42) * mm});
            skPoint(sketch, "E45.center", {"position": v(0, 0) * mm});
            skSolve(sketch);
        }
        {
            var Q0;
            Q0=makeQuery(id+"F4.imprint","IMPRINT",FACE,{"disambiguationData":[TD([[makeQuery(id+"F4.imprint","IMPRINT",EDGE,{"derivedFrom":sQuery(id+"F4.wireOp",EDGE,"E34.0")}),1.0]])]});
            extrude(context, id + "F5", {"entities" : qUnion([Q0]), "depth" : 0.5 * mm, "offsetDistance" : 25 * mm});
        }
        {
            var Q0;
            Q0=makeQuery(id+"F5.opExtrude","SWEPT_EDGE",EDGE,{"disambiguationData":[OSD([sQuery(id+"F4.wireOp",EDGE,"E45.2.2"),sQuery(id+"F4.wireOp",EDGE,"E45.2.3")])]});
            var Q1;
            Q1=makeQuery(id+"F5.opExtrude","SWEPT_EDGE",EDGE,{"disambiguationData":[OSD([sQuery(id+"F4.wireOp",EDGE,"E45.1.2"),sQuery(id+"F4.wireOp",EDGE,"E45.1.3")])]});
            var Q2;
            Q2=makeQuery(id+"F5.opExtrude","SWEPT_EDGE",EDGE,{"disambiguationData":[OSD([sQuery(id+"F4.wireOp",EDGE,"E41"),sQuery(id+"F4.wireOp",EDGE,"E42.right")])]});
            var Q3;
            Q3=makeQuery(id+"F5.opExtrude","SWEPT_EDGE",EDGE,{"disambiguationData":[OSD([sQuery(id+"F4.wireOp",EDGE,"E45.1.0"),sQuery(id+"F4.wireOp",EDGE,"E45.1.2")])]});
            var Q4;
            Q4=makeQuery(id+"F5.opExtrude","SWEPT_EDGE",EDGE,{"disambiguationData":[OSD([sQuery(id+"F4.wireOp",EDGE,"E41"),sQuery(id+"F4.wireOp",EDGE,"E44")])]});
            var Q5;
            Q5=makeQuery(id+"F5.opExtrude","SWEPT_EDGE",EDGE,{"disambiguationData":[OSD([sQuery(id+"F4.wireOp",EDGE,"E45.2.0"),sQuery(id+"F4.wireOp",EDGE,"E45.2.2")])]});
            fillet(context, id + "F6", {"entities" : qUnion([Q0, Q1, Q2, Q3, Q4, Q5]), "radius" : 2 * mm, "tangentPropagation" : true, "allowEdgeOverflow" : false});
        }
        {
            var Q0;
            Q0=makeQuery(id+"F3.opExtrude","SWEPT_EDGE",EDGE,{"disambiguationData":[OSD([sQuery(id+"F2.wireOp",EDGE,"E14.2"),sQuery(id+"F2.wireOp",EDGE,"E15")])]});
            var Q1;
            Q1=makeQuery(id+"F3.opExtrude","SWEPT_EDGE",EDGE,{"disambiguationData":[OSD([sQuery(id+"F2.wireOp",EDGE,"E26.3.0"),sQuery(id+"F2.wireOp",EDGE,"E26.3.1")])]});
            var Q2;
            Q2=makeQuery(id+"F3.opExtrude","SWEPT_EDGE",EDGE,{"disambiguationData":[OSD([sQuery(id+"F2.wireOp",EDGE,"E26.2.0"),sQuery(id+"F2.wireOp",EDGE,"E26.2.1")])]});
            var Q3;
            Q3=makeQuery(id+"F3.opExtrude","SWEPT_EDGE",EDGE,{"disambiguationData":[OSD([sQuery(id+"F2.wireOp",EDGE,"E26.1.0"),sQuery(id+"F2.wireOp",EDGE,"E26.1.1")])]});
            fillet(context, id + "F7", {"entities" : qUnion([Q0, Q1, Q2, Q3]), "radius" : 2 * mm, "tangentPropagation" : true, "allowEdgeOverflow" : false});
        }
        {
            var Q0;
            Q0=qCreatedBy(makeId("Right.planeOp"),FACE);
            var sketch = newSketch(context, id + "F8", { "sketchPlane" : qUnion([Q0])});
            skLineSegment(sketch, "E46.0", {"start": v(-11.37, 20.65) * mm, "end": v(11.37, 20.65) * mm});
            skLineSegment(sketch, "E46.1", {"start": v(16.12, 17.2) * mm, "end": v(23.15, -4.43) * mm});
            skLineSegment(sketch, "E46.2", {"start": v(21.33, -10.02) * mm, "end": v(2.94, -23.38) * mm});
            skLineSegment(sketch, "E46.3", {"start": v(-2.94, -23.38) * mm, "end": v(-21.33, -10.02) * mm});
            skLineSegment(sketch, "E46.4", {"start": v(-23.15, -4.43) * mm, "end": v(-16.12, 17.2) * mm});
            skPoint(sketch, "E46.0.midPoint", {"position": v(0, 20.65) * mm});
            skPoint(sketch, "E47.visualSharp", {"position": v(-25.9, 35.65) * mm});
            skArc(sketch, "E47.filletArc", {"start": v(-22.27, 35.65) * mm, "mid": v(-25.2, 34.7) * mm, "end": v(-27.02, 32.2) * mm});
            skPoint(sketch, "E48.visualSharp", {"position": v(25.9, 35.65) * mm});
            skArc(sketch, "E48.filletArc", {"start": v(27.02, 32.2) * mm, "mid": v(25.2, 34.7) * mm, "end": v(22.27, 35.65) * mm});
            skPoint(sketch, "E49.visualSharp", {"position": v(15, 20.65) * mm});
            skArc(sketch, "E49.filletArc", {"start": v(16.12, 17.2) * mm, "mid": v(14.3, 19.7) * mm, "end": v(11.37, 20.65) * mm});
            skPoint(sketch, "E50.visualSharp", {"position": v(-15, 20.65) * mm});
            skArc(sketch, "E50.filletArc", {"start": v(-11.37, 20.65) * mm, "mid": v(-14.3, 19.7) * mm, "end": v(-16.12, 17.2) * mm});
            skPoint(sketch, "E51.visualSharp", {"position": v(-24.27, -7.89) * mm});
            skArc(sketch, "E51.filletArc", {"start": v(-23.15, -4.43) * mm, "mid": v(-23.15, -7.52) * mm, "end": v(-21.33, -10.02) * mm});
            skPoint(sketch, "E52.visualSharp", {"position": v(0, -25.52) * mm});
            skArc(sketch, "E52.filletArc", {"start": v(-2.94, -23.38) * mm, "mid": v(0, -24.34) * mm, "end": v(2.94, -23.38) * mm});
            skPoint(sketch, "E53.visualSharp", {"position": v(24.27, -7.89) * mm});
            skArc(sketch, "E53.filletArc", {"start": v(21.33, -10.02) * mm, "mid": v(23.15, -7.52) * mm, "end": v(23.15, -4.43) * mm});
            skPoint(sketch, "E54.visualSharp", {"position": v(41.9, -13.62) * mm});
            skArc(sketch, "E54.filletArc", {"start": v(38.97, -15.75) * mm, "mid": v(40.78, -13.25) * mm, "end": v(40.78, -10.16) * mm});
            skPoint(sketch, "E55.visualSharp", {"position": v(0, -44.06) * mm});
            skArc(sketch, "E55.filletArc", {"start": v(-2.94, -41.93) * mm, "mid": v(0, -42.88) * mm, "end": v(2.94, -41.93) * mm});
            skPoint(sketch, "E56.visualSharp", {"position": v(-41.9, -13.62) * mm});
            skArc(sketch, "E56.filletArc", {"start": v(-40.78, -10.16) * mm, "mid": v(-40.78, -13.25) * mm, "end": v(-38.97, -15.75) * mm});
            skArc(sketch, "E57", {"start": v(15, 35.65) * mm, "mid": v(0.25, 50.64) * mm, "end": v(-15, 36.15) * mm});
            skLineSegment(sketch, "E58.top", {"start": v(0, 36.15) * mm, "end": v(-15, 36.15) * mm});
            skLineSegment(sketch, "E58.left", {"start": v(0, 35.65) * mm, "end": v(0, 36.15) * mm});
            skLineSegment(sketch, "E59", {"start": v(-22.27, 35.65) * mm, "end": v(0, 35.65) * mm});
            skLineSegment(sketch, "E60", {"start": v(15, 35.65) * mm, "end": v(22.27, 35.65) * mm});
            skLineSegment(sketch, "E61.1.0", {"start": v(-40.78, -10.16) * mm, "end": v(-33.9, 11.02) * mm});
            skArc(sketch, "E61.1.1", {"start": v(-29.27, 25.28) * mm, "mid": v(-48.09, 15.89) * mm, "end": v(-39, -3.09) * mm});
            skLineSegment(sketch, "E61.1.2", {"start": v(-34.38, 11.17) * mm, "end": v(-39, -3.09) * mm});
            skLineSegment(sketch, "E61.1.3", {"start": v(-29.27, 25.28) * mm, "end": v(-27.02, 32.2) * mm});
            skLineSegment(sketch, "E61.2.0", {"start": v(-2.94, -41.93) * mm, "end": v(-20.95, -28.84) * mm});
            skArc(sketch, "E61.2.1", {"start": v(-33.09, -20.02) * mm, "mid": v(-29.97, -40.82) * mm, "end": v(-9.12, -38.05) * mm});
            skLineSegment(sketch, "E61.2.2", {"start": v(-21.25, -29.24) * mm, "end": v(-9.12, -38.05) * mm});
            skLineSegment(sketch, "E61.2.3", {"start": v(-33.09, -20.02) * mm, "end": v(-38.97, -15.75) * mm});
            skLineSegment(sketch, "E61.3.0", {"start": v(38.97, -15.75) * mm, "end": v(20.95, -28.84) * mm});
            skArc(sketch, "E61.3.1", {"start": v(8.82, -37.65) * mm, "mid": v(29.57, -41.12) * mm, "end": v(33.37, -20.43) * mm});
            skLineSegment(sketch, "E61.3.2", {"start": v(21.25, -29.24) * mm, "end": v(33.37, -20.43) * mm});
            skLineSegment(sketch, "E61.3.3", {"start": v(8.82, -37.65) * mm, "end": v(2.94, -41.93) * mm});
            skLineSegment(sketch, "E61.4.0", {"start": v(27.02, 32.2) * mm, "end": v(33.9, 11.02) * mm});
            skArc(sketch, "E61.4.1", {"start": v(38.54, -3.25) * mm, "mid": v(48.24, 15.41) * mm, "end": v(29.74, 25.43) * mm});
            skLineSegment(sketch, "E61.4.2", {"start": v(34.38, 11.17) * mm, "end": v(29.74, 25.43) * mm});
            skLineSegment(sketch, "E61.4.3", {"start": v(38.54, -3.25) * mm, "end": v(40.78, -10.16) * mm});
            skPoint(sketch, "E61.center", {"position": v(0, 0) * mm});
            skLineSegment(sketch, "E62", {"start": v(-34.38, 11.17) * mm, "end": v(-33.9, 11.02) * mm});
            skLineSegment(sketch, "E63", {"start": v(-21.25, -29.24) * mm, "end": v(-20.95, -28.84) * mm});
            skLineSegment(sketch, "E64", {"start": v(20.95, -28.84) * mm, "end": v(21.25, -29.24) * mm});
            skLineSegment(sketch, "E65", {"start": v(33.9, 11.02) * mm, "end": v(34.38, 11.17) * mm});
            skSolve(sketch);
        }
        {
            var Q0;
            Q0=makeQuery(id+"F8.imprint","IMPRINT",FACE,{"disambiguationData":[TD([[makeQuery(id+"F8.imprint","IMPRINT",EDGE,{"derivedFrom":sQuery(id+"F8.wireOp",EDGE,"E46.0")}),1.0]])]});
            extrude(context, id + "F9", {"entities" : qUnion([Q0]), "depth" : 0.5 * mm, "offsetDistance" : 25 * mm});
        }
        {
            var Q0;
            Q0=makeQuery(id+"F9.opExtrude","SWEPT_EDGE",EDGE,{"disambiguationData":[OSD([sQuery(id+"F8.wireOp",EDGE,"E61.2.1"),sQuery(id+"F8.wireOp",EDGE,"E61.2.2")])]});
            var Q1;
            Q1=makeQuery(id+"F9.opExtrude","SWEPT_EDGE",EDGE,{"disambiguationData":[OSD([sQuery(id+"F8.wireOp",EDGE,"E61.1.1"),sQuery(id+"F8.wireOp",EDGE,"E61.1.2")])]});
            var Q2;
            Q2=makeQuery(id+"F9.opExtrude","SWEPT_EDGE",EDGE,{"disambiguationData":[OSD([sQuery(id+"F8.wireOp",EDGE,"E57"),sQuery(id+"F8.wireOp",EDGE,"E60")])]});
            var Q3;
            Q3=makeQuery(id+"F9.opExtrude","SWEPT_EDGE",EDGE,{"disambiguationData":[OSD([sQuery(id+"F8.wireOp",EDGE,"E61.3.1"),sQuery(id+"F8.wireOp",EDGE,"E61.3.2")])]});
            var Q4;
            Q4=makeQuery(id+"F9.opExtrude","SWEPT_EDGE",EDGE,{"disambiguationData":[OSD([sQuery(id+"F8.wireOp",EDGE,"E61.4.1"),sQuery(id+"F8.wireOp",EDGE,"E61.4.3")])]});
            var Q5;
            Q5=makeQuery(id+"F9.opExtrude","SWEPT_EDGE",EDGE,{"disambiguationData":[OSD([sQuery(id+"F8.wireOp",EDGE,"E61.4.1"),sQuery(id+"F8.wireOp",EDGE,"E61.4.2")])]});
            var Q6;
            Q6=makeQuery(id+"F9.opExtrude","SWEPT_EDGE",EDGE,{"disambiguationData":[OSD([sQuery(id+"F8.wireOp",EDGE,"E61.3.1"),sQuery(id+"F8.wireOp",EDGE,"E61.3.3")])]});
            var Q7;
            Q7=makeQuery(id+"F9.opExtrude","SWEPT_EDGE",EDGE,{"disambiguationData":[OSD([sQuery(id+"F8.wireOp",EDGE,"E57"),sQuery(id+"F8.wireOp",EDGE,"E58.top")])]});
            var Q8;
            Q8=makeQuery(id+"F9.opExtrude","SWEPT_EDGE",EDGE,{"disambiguationData":[OSD([sQuery(id+"F8.wireOp",EDGE,"E61.1.1"),sQuery(id+"F8.wireOp",EDGE,"E61.1.3")])]});
            var Q9;
            Q9=makeQuery(id+"F9.opExtrude","SWEPT_EDGE",EDGE,{"disambiguationData":[OSD([sQuery(id+"F8.wireOp",EDGE,"E61.2.1"),sQuery(id+"F8.wireOp",EDGE,"E61.2.3")])]});
            fillet(context, id + "F10", {"entities" : qUnion([Q0, Q1, Q2, Q3, Q4, Q5, Q6, Q7, Q8, Q9]), "radius" : 2 * mm, "tangentPropagation" : true, "allowEdgeOverflow" : false});
        }
        {
            var Q0;
            Q0=makeQuery(id+"F9.opExtrude","SWEPT_BODY",BODY,{"disambiguationData":[OSD([sQuery(id+"F8.wireOp",EDGE,"E46.0"),sQuery(id+"F8.wireOp",EDGE,"E46.1"),sQuery(id+"F8.wireOp",EDGE,"E46.2"),sQuery(id+"F8.wireOp",EDGE,"E46.3"),sQuery(id+"F8.wireOp",EDGE,"E46.4"),sQuery(id+"F8.wireOp",EDGE,"E47.filletArc"),sQuery(id+"F8.wireOp",EDGE,"E48.filletArc"),sQuery(id+"F8.wireOp",EDGE,"E49.filletArc"),sQuery(id+"F8.wireOp",EDGE,"E50.filletArc"),sQuery(id+"F8.wireOp",EDGE,"E51.filletArc"),sQuery(id+"F8.wireOp",EDGE,"E52.filletArc"),sQuery(id+"F8.wireOp",EDGE,"E53.filletArc"),sQuery(id+"F8.wireOp",EDGE,"E54.filletArc"),sQuery(id+"F8.wireOp",EDGE,"E55.filletArc"),sQuery(id+"F8.wireOp",EDGE,"E56.filletArc"),sQuery(id+"F8.wireOp",EDGE,"E57"),sQuery(id+"F8.wireOp",EDGE,"E58.top"),sQuery(id+"F8.wireOp",EDGE,"E58.left"),sQuery(id+"F8.wireOp",EDGE,"E59"),sQuery(id+"F8.wireOp",EDGE,"E60"),sQuery(id+"F8.wireOp",EDGE,"E61.1.0"),sQuery(id+"F8.wireOp",EDGE,"E61.1.1"),sQuery(id+"F8.wireOp",EDGE,"E61.1.2"),sQuery(id+"F8.wireOp",EDGE,"E61.1.3"),sQuery(id+"F8.wireOp",EDGE,"E61.2.0"),sQuery(id+"F8.wireOp",EDGE,"E61.2.1"),sQuery(id+"F8.wireOp",EDGE,"E61.2.2"),sQuery(id+"F8.wireOp",EDGE,"E61.2.3"),sQuery(id+"F8.wireOp",EDGE,"E61.3.0"),sQuery(id+"F8.wireOp",EDGE,"E61.3.1"),sQuery(id+"F8.wireOp",EDGE,"E61.3.2"),sQuery(id+"F8.wireOp",EDGE,"E61.3.3"),sQuery(id+"F8.wireOp",EDGE,"E61.4.0"),sQuery(id+"F8.wireOp",EDGE,"E61.4.1"),sQuery(id+"F8.wireOp",EDGE,"E61.4.2"),sQuery(id+"F8.wireOp",EDGE,"E61.4.3"),sQuery(id+"F8.wireOp",EDGE,"E62"),sQuery(id+"F8.wireOp",EDGE,"E63"),sQuery(id+"F8.wireOp",EDGE,"E64"),sQuery(id+"F8.wireOp",EDGE,"E65")])]});
            var Q1;
            Q1=qCreatedBy(makeId("Origin.pointOp"),VERTEX);
            transform(context, id + "F11", {"entities" : qUnion([Q0]), "transformType" : TransformType.SCALE_UNIFORMLY, "scale" : 0.5, "scalePoint" : qUnion([Q1]), "makeCopy" : false});
        }
        {
            var Q0;
            Q0=makeQuery(id+"F5.opExtrude","SWEPT_BODY",BODY,{"disambiguationData":[OSD([sQuery(id+"F4.wireOp",EDGE,"E34.0"),sQuery(id+"F4.wireOp",EDGE,"E34.1"),sQuery(id+"F4.wireOp",EDGE,"E34.2"),sQuery(id+"F4.wireOp",EDGE,"E35.filletArc"),sQuery(id+"F4.wireOp",EDGE,"E36.filletArc"),sQuery(id+"F4.wireOp",EDGE,"E37.filletArc"),sQuery(id+"F4.wireOp",EDGE,"E38.filletArc"),sQuery(id+"F4.wireOp",EDGE,"E39.filletArc"),sQuery(id+"F4.wireOp",EDGE,"E40.filletArc"),sQuery(id+"F4.wireOp",EDGE,"E41"),sQuery(id+"F4.wireOp",EDGE,"E42.bottom"),sQuery(id+"F4.wireOp",EDGE,"E42.right"),sQuery(id+"F4.wireOp",EDGE,"E43"),sQuery(id+"F4.wireOp",EDGE,"E44"),sQuery(id+"F4.wireOp",EDGE,"E45.1.0"),sQuery(id+"F4.wireOp",EDGE,"E45.1.1"),sQuery(id+"F4.wireOp",EDGE,"E45.1.2"),sQuery(id+"F4.wireOp",EDGE,"E45.1.3"),sQuery(id+"F4.wireOp",EDGE,"E45.1.4"),sQuery(id+"F4.wireOp",EDGE,"E45.2.0"),sQuery(id+"F4.wireOp",EDGE,"E45.2.1"),sQuery(id+"F4.wireOp",EDGE,"E45.2.2"),sQuery(id+"F4.wireOp",EDGE,"E45.2.3"),sQuery(id+"F4.wireOp",EDGE,"E45.2.4")])]});
            var Q1;
            Q1=qCreatedBy(makeId("Origin.pointOp"),VERTEX);
            transform(context, id + "F12", {"entities" : qUnion([Q0]), "transformType" : TransformType.SCALE_UNIFORMLY, "scale" : 0.5, "scalePoint" : qUnion([Q1]), "makeCopy" : false});
        }
        {
            var Q0;
            Q0=makeQuery(id+"F3.opExtrude","SWEPT_BODY",BODY,{"disambiguationData":[OSD([sQuery(id+"F2.wireOp",EDGE,"E13.bottom"),sQuery(id+"F2.wireOp",EDGE,"E13.top"),sQuery(id+"F2.wireOp",EDGE,"E13.left"),sQuery(id+"F2.wireOp",EDGE,"E13.right"),sQuery(id+"F2.wireOp",EDGE,"E14.2"),sQuery(id+"F2.wireOp",EDGE,"E15"),sQuery(id+"F2.wireOp",EDGE,"E16.trimOffspring"),sQuery(id+"F2.wireOp",EDGE,"E17.left"),sQuery(id+"F2.wireOp",EDGE,"E17.right"),sQuery(id+"F2.wireOp",EDGE,"E18.filletArc"),sQuery(id+"F2.wireOp",EDGE,"E19.filletArc"),sQuery(id+"F2.wireOp",EDGE,"E20.filletArc"),sQuery(id+"F2.wireOp",EDGE,"E21.filletArc"),sQuery(id+"F2.wireOp",EDGE,"E22.filletArc"),sQuery(id+"F2.wireOp",EDGE,"E23.filletArc"),sQuery(id+"F2.wireOp",EDGE,"E24.filletArc"),sQuery(id+"F2.wireOp",EDGE,"E25.filletArc"),sQuery(id+"F2.wireOp",EDGE,"E26.1.0"),sQuery(id+"F2.wireOp",EDGE,"E26.1.1"),sQuery(id+"F2.wireOp",EDGE,"E26.1.2"),sQuery(id+"F2.wireOp",EDGE,"E26.1.4"),sQuery(id+"F2.wireOp",EDGE,"E26.2.0"),sQuery(id+"F2.wireOp",EDGE,"E26.2.1"),sQuery(id+"F2.wireOp",EDGE,"E26.2.2"),sQuery(id+"F2.wireOp",EDGE,"E26.2.3"),sQuery(id+"F2.wireOp",EDGE,"E26.2.4"),sQuery(id+"F2.wireOp",EDGE,"E26.2.5"),sQuery(id+"F2.wireOp",EDGE,"E26.3.0"),sQuery(id+"F2.wireOp",EDGE,"E26.3.1"),sQuery(id+"F2.wireOp",EDGE,"E26.3.2"),sQuery(id+"F2.wireOp",EDGE,"E26.3.4"),sQuery(id+"F2.wireOp",EDGE,"E27"),sQuery(id+"F2.wireOp",EDGE,"E28"),sQuery(id+"F2.wireOp",EDGE,"E29.filletArc"),sQuery(id+"F2.wireOp",EDGE,"E30.filletArc"),sQuery(id+"F2.wireOp",EDGE,"E31.filletArc"),sQuery(id+"F2.wireOp",EDGE,"E32.filletArc"),sQuery(id+"F2.wireOp",EDGE,"E33")])]});
            var Q1;
            Q1=qCreatedBy(makeId("Origin.pointOp"),VERTEX);
            transform(context, id + "F13", {"entities" : qUnion([Q0]), "transformType" : TransformType.SCALE_UNIFORMLY, "scale" : 0.5, "scalePoint" : qUnion([Q1]), "makeCopy" : false});
        }
        {
            var Q0;
            Q0=qCreatedBy(makeId("Top.planeOp"),FACE);
            var sketch = newSketch(context, id + "F14", { "sketchPlane" : qUnion([Q0])});
            skArc(sketch, "E66", {"start": v(0, 50) * mm, "mid": v(-35.36, 35.36) * mm, "end": v(-50, 0) * mm});
            skPoint(sketch, "E67", {"position": v(0, 50) * mm});
            skPoint(sketch, "E68", {"position": v(50, 0) * mm});
            skPoint(sketch, "E69", {"position": v(0, -50) * mm});
            skPoint(sketch, "E70", {"position": v(-50, 0) * mm});
            skArc(sketch, "E71.trimOffspring", {"start": v(0, -50) * mm, "mid": v(35.36, -35.36) * mm, "end": v(50, 0) * mm});
            skSolve(sketch);
        }
        {
            var Q0;
            Q0=makeQuery(id+"F5.opExtrude","SWEPT_BODY",BODY,{"disambiguationData":[OSD([sQuery(id+"F4.wireOp",EDGE,"E34.0"),sQuery(id+"F4.wireOp",EDGE,"E34.1"),sQuery(id+"F4.wireOp",EDGE,"E34.2"),sQuery(id+"F4.wireOp",EDGE,"E35.filletArc"),sQuery(id+"F4.wireOp",EDGE,"E36.filletArc"),sQuery(id+"F4.wireOp",EDGE,"E37.filletArc"),sQuery(id+"F4.wireOp",EDGE,"E38.filletArc"),sQuery(id+"F4.wireOp",EDGE,"E39.filletArc"),sQuery(id+"F4.wireOp",EDGE,"E40.filletArc"),sQuery(id+"F4.wireOp",EDGE,"E41"),sQuery(id+"F4.wireOp",EDGE,"E42.bottom"),sQuery(id+"F4.wireOp",EDGE,"E42.right"),sQuery(id+"F4.wireOp",EDGE,"E43"),sQuery(id+"F4.wireOp",EDGE,"E44"),sQuery(id+"F4.wireOp",EDGE,"E45.1.0"),sQuery(id+"F4.wireOp",EDGE,"E45.1.1"),sQuery(id+"F4.wireOp",EDGE,"E45.1.2"),sQuery(id+"F4.wireOp",EDGE,"E45.1.3"),sQuery(id+"F4.wireOp",EDGE,"E45.1.4"),sQuery(id+"F4.wireOp",EDGE,"E45.2.0"),sQuery(id+"F4.wireOp",EDGE,"E45.2.1"),sQuery(id+"F4.wireOp",EDGE,"E45.2.2"),sQuery(id+"F4.wireOp",EDGE,"E45.2.3"),sQuery(id+"F4.wireOp",EDGE,"E45.2.4")])]});
            var Q1;
            Q1=qCreatedBy(makeId("Origin.pointOp"),VERTEX);
            transform(context, id + "F15", {"entities" : qUnion([Q0]), "transformType" : TransformType.SCALE_UNIFORMLY, "scale" : 1.25, "scalePoint" : qUnion([Q1]), "makeCopy" : true});
        }
        {
            var Q0;
            Q0=makeQuery(id+"F15.opPattern","COPY",BODY,{"derivedFrom":makeQuery(id+"F5.opExtrude","SWEPT_BODY",BODY,{"disambiguationData":[OSD([sQuery(id+"F4.wireOp",EDGE,"E34.0"),sQuery(id+"F4.wireOp",EDGE,"E34.1"),sQuery(id+"F4.wireOp",EDGE,"E34.2"),sQuery(id+"F4.wireOp",EDGE,"E35.filletArc"),sQuery(id+"F4.wireOp",EDGE,"E36.filletArc"),sQuery(id+"F4.wireOp",EDGE,"E37.filletArc"),sQuery(id+"F4.wireOp",EDGE,"E38.filletArc"),sQuery(id+"F4.wireOp",EDGE,"E39.filletArc"),sQuery(id+"F4.wireOp",EDGE,"E40.filletArc"),sQuery(id+"F4.wireOp",EDGE,"E41"),sQuery(id+"F4.wireOp",EDGE,"E42.bottom"),sQuery(id+"F4.wireOp",EDGE,"E42.right"),sQuery(id+"F4.wireOp",EDGE,"E43"),sQuery(id+"F4.wireOp",EDGE,"E44"),sQuery(id+"F4.wireOp",EDGE,"E45.1.0"),sQuery(id+"F4.wireOp",EDGE,"E45.1.1"),sQuery(id+"F4.wireOp",EDGE,"E45.1.2"),sQuery(id+"F4.wireOp",EDGE,"E45.1.3"),sQuery(id+"F4.wireOp",EDGE,"E45.1.4"),sQuery(id+"F4.wireOp",EDGE,"E45.2.0"),sQuery(id+"F4.wireOp",EDGE,"E45.2.1"),sQuery(id+"F4.wireOp",EDGE,"E45.2.2"),sQuery(id+"F4.wireOp",EDGE,"E45.2.3"),sQuery(id+"F4.wireOp",EDGE,"E45.2.4")])]}),"instanceName":"1"});
            var Q1;
            Q1=qCreatedBy(makeId("Origin.pointOp"),VERTEX);
            transform(context, id + "F16", {"entities" : qUnion([Q0]), "transformType" : TransformType.SCALE_UNIFORMLY, "scale" : 1.25, "scalePoint" : qUnion([Q1]), "makeCopy" : true});
        }
        {
            var Q0;
            Q0=makeQuery(id+"F9.opExtrude","SWEPT_BODY",BODY,{"disambiguationData":[OSD([sQuery(id+"F8.wireOp",EDGE,"E46.0"),sQuery(id+"F8.wireOp",EDGE,"E46.1"),sQuery(id+"F8.wireOp",EDGE,"E46.2"),sQuery(id+"F8.wireOp",EDGE,"E46.3"),sQuery(id+"F8.wireOp",EDGE,"E46.4"),sQuery(id+"F8.wireOp",EDGE,"E47.filletArc"),sQuery(id+"F8.wireOp",EDGE,"E48.filletArc"),sQuery(id+"F8.wireOp",EDGE,"E49.filletArc"),sQuery(id+"F8.wireOp",EDGE,"E50.filletArc"),sQuery(id+"F8.wireOp",EDGE,"E51.filletArc"),sQuery(id+"F8.wireOp",EDGE,"E52.filletArc"),sQuery(id+"F8.wireOp",EDGE,"E53.filletArc"),sQuery(id+"F8.wireOp",EDGE,"E54.filletArc"),sQuery(id+"F8.wireOp",EDGE,"E55.filletArc"),sQuery(id+"F8.wireOp",EDGE,"E56.filletArc"),sQuery(id+"F8.wireOp",EDGE,"E57"),sQuery(id+"F8.wireOp",EDGE,"E58.top"),sQuery(id+"F8.wireOp",EDGE,"E58.left"),sQuery(id+"F8.wireOp",EDGE,"E59"),sQuery(id+"F8.wireOp",EDGE,"E60"),sQuery(id+"F8.wireOp",EDGE,"E61.1.0"),sQuery(id+"F8.wireOp",EDGE,"E61.1.1"),sQuery(id+"F8.wireOp",EDGE,"E61.1.2"),sQuery(id+"F8.wireOp",EDGE,"E61.1.3"),sQuery(id+"F8.wireOp",EDGE,"E61.2.0"),sQuery(id+"F8.wireOp",EDGE,"E61.2.1"),sQuery(id+"F8.wireOp",EDGE,"E61.2.2"),sQuery(id+"F8.wireOp",EDGE,"E61.2.3"),sQuery(id+"F8.wireOp",EDGE,"E61.3.0"),sQuery(id+"F8.wireOp",EDGE,"E61.3.1"),sQuery(id+"F8.wireOp",EDGE,"E61.3.2"),sQuery(id+"F8.wireOp",EDGE,"E61.3.3"),sQuery(id+"F8.wireOp",EDGE,"E61.4.0"),sQuery(id+"F8.wireOp",EDGE,"E61.4.1"),sQuery(id+"F8.wireOp",EDGE,"E61.4.2"),sQuery(id+"F8.wireOp",EDGE,"E61.4.3"),sQuery(id+"F8.wireOp",EDGE,"E62"),sQuery(id+"F8.wireOp",EDGE,"E63"),sQuery(id+"F8.wireOp",EDGE,"E64"),sQuery(id+"F8.wireOp",EDGE,"E65")])]});
            var Q1;
            Q1=qCreatedBy(makeId("Origin.pointOp"),VERTEX);
            transform(context, id + "F17", {"entities" : qUnion([Q0]), "transformType" : TransformType.SCALE_UNIFORMLY, "scale" : 1.8, "scalePoint" : qUnion([Q1]), "makeCopy" : true});
        }
        {
            var Q0;
            Q0=qCreatedBy(makeId("Front.planeOp"),FACE);
            var sketch = newSketch(context, id + "F18", { "sketchPlane" : qUnion([Q0])});
            skLineSegment(sketch, "E72.bottom", {"start": v(50.6, 3.54) * mm, "end": v(43.54, 10.6) * mm});
            skLineSegment(sketch, "E72.top", {"start": v(36.46, -10.6) * mm, "end": v(29.4, -3.54) * mm});
            skLineSegment(sketch, "E72.left", {"start": v(50.6, -3.54) * mm, "end": v(43.54, -10.6) * mm});
            skLineSegment(sketch, "E72.right", {"start": v(36.46, 10.6) * mm, "end": v(29.4, 3.54) * mm});
            skPoint(sketch, "E72.middle", {"position": v(40, 0) * mm});
            skLineSegment(sketch, "E73.MirrorCS", {"start": v(-50.6, -3.54) * mm, "end": v(-43.54, -10.6) * mm});
            skLineSegment(sketch, "E74.MirrorCS", {"start": v(-36.46, 10.6) * mm, "end": v(-29.4, 3.54) * mm});
            skLineSegment(sketch, "E75.MirrorCS", {"start": v(-50.6, 3.54) * mm, "end": v(-43.54, 10.6) * mm});
            skPoint(sketch, "E76.MirrorP", {"position": v(-40, 0) * mm});
            skLineSegment(sketch, "E77.MirrorCS", {"start": v(-36.46, -10.6) * mm, "end": v(-29.4, -3.54) * mm});
            skLineSegment(sketch, "E78", {"start": v(0, 0) * mm, "end": v(0, 40) * mm, "construction": true});
            skLineSegment(sketch, "E79", {"start": v(0, 0) * mm, "end": v(-23.88, 0) * mm, "construction": true});
            skPoint(sketch, "E80.visualSharp", {"position": v(40, 14.14) * mm});
            skArc(sketch, "E80.filletArc", {"start": v(43.54, 10.6) * mm, "mid": v(40, 12.07) * mm, "end": v(36.46, 10.6) * mm});
            skPoint(sketch, "E81.visualSharp", {"position": v(25.86, 0) * mm});
            skArc(sketch, "E81.filletArc", {"start": v(29.4, 3.54) * mm, "mid": v(27.93, 0) * mm, "end": v(29.4, -3.54) * mm});
            skPoint(sketch, "E82.visualSharp", {"position": v(40, -14.14) * mm});
            skArc(sketch, "E82.filletArc", {"start": v(36.46, -10.6) * mm, "mid": v(40, -12.07) * mm, "end": v(43.54, -10.6) * mm});
            skPoint(sketch, "E83.visualSharp", {"position": v(54.14, 0) * mm});
            skArc(sketch, "E83.filletArc", {"start": v(50.6, -3.54) * mm, "mid": v(52.07, 0) * mm, "end": v(50.6, 3.54) * mm});
            skPoint(sketch, "E84.visualSharp", {"position": v(-40, 14.14) * mm});
            skArc(sketch, "E84.filletArc", {"start": v(-36.46, 10.6) * mm, "mid": v(-40, 12.07) * mm, "end": v(-43.54, 10.6) * mm});
            skPoint(sketch, "E85.visualSharp", {"position": v(-25.86, 0) * mm});
            skArc(sketch, "E85.filletArc", {"start": v(-29.4, -3.54) * mm, "mid": v(-27.93, 0) * mm, "end": v(-29.4, 3.54) * mm});
            skPoint(sketch, "E86.visualSharp", {"position": v(-40, -14.14) * mm});
            skArc(sketch, "E86.filletArc", {"start": v(-43.54, -10.6) * mm, "mid": v(-40, -12.07) * mm, "end": v(-36.46, -10.6) * mm});
            skPoint(sketch, "E87.visualSharp", {"position": v(-54.14, 0) * mm});
            skArc(sketch, "E87.filletArc", {"start": v(-50.6, 3.54) * mm, "mid": v(-52.07, 0) * mm, "end": v(-50.6, -3.54) * mm});
            skSolve(sketch);
        }
        {
            var Q0;
            Q0=qCreatedBy(makeId("Right.planeOp"),FACE);
            var sketch = newSketch(context, id + "F19", { "sketchPlane" : qUnion([Q0])});
            skLineSegment(sketch, "E88.bottom", {"start": v(30, 10) * mm, "end": v(50, 10) * mm});
            skLineSegment(sketch, "E88.top", {"start": v(30, -10) * mm, "end": v(50, -10) * mm});
            skLineSegment(sketch, "E88.left", {"start": v(30, 10) * mm, "end": v(30, -10) * mm});
            skLineSegment(sketch, "E88.right", {"start": v(50, 10) * mm, "end": v(50, -10) * mm});
            skPoint(sketch, "E88.middle", {"position": v(40, 0) * mm});
            skLineSegment(sketch, "E89.MirrorCS", {"start": v(-50, 10) * mm, "end": v(-50, -10) * mm});
            skPoint(sketch, "E90.MirrorP", {"position": v(-40, 0) * mm});
            skLineSegment(sketch, "E91.MirrorCS", {"start": v(-30, 10) * mm, "end": v(-30, -10) * mm});
            skLineSegment(sketch, "E92.MirrorCS", {"start": v(-30, -10) * mm, "end": v(-50, -10) * mm});
            skLineSegment(sketch, "E93.MirrorCS", {"start": v(-30, 10) * mm, "end": v(-50, 10) * mm});
            skSolve(sketch);
        }
        {
            var Q0;
            Q0=makeQuery(id+"F18.imprint","IMPRINT",FACE,{"disambiguationData":[TD([[makeQuery(id+"F18.imprint","IMPRINT",EDGE,{"derivedFrom":sQuery(id+"F18.wireOp",EDGE,"E72.bottom")}),1.0]])]});
            var Q1;
            Q1=makeQuery(id+"F18.imprint","IMPRINT",FACE,{"disambiguationData":[TD([[makeQuery(id+"F18.imprint","IMPRINT",EDGE,{"derivedFrom":sQuery(id+"F18.wireOp",EDGE,"E73.MirrorCS")}),1.0]])]});
            extrude(context, id + "F20", {"entities" : qUnion([Q0, Q1]), "endBound" : BoundingType.SYMMETRIC, "depth" : 5 * mm, "offsetDistance" : 25 * mm});
        }
        {
            var Q0;
            Q0=sQuery(id+"F14.wireOp",EDGE,"E71.trimOffspring");
            var Q1;
            Q1=makeQuery(id+"F19.imprint","IMPRINT",FACE,{"disambiguationData":[TD([[makeQuery(id+"F19.imprint","IMPRINT",EDGE,{"derivedFrom":sQuery(id+"F19.wireOp",EDGE,"E89.MirrorCS")}),1.0]])]});
            var Q2;
            Q2=makeQuery(id+"F18.imprint","IMPRINT",FACE,{"disambiguationData":[TD([[makeQuery(id+"F18.imprint","IMPRINT",EDGE,{"derivedFrom":sQuery(id+"F18.wireOp",EDGE,"E72.bottom")}),1.0]])]});
            loft(context, id + "F21", {"addSections" : true, "spine" : qUnion([Q0]), "sectionCount" : 50, "startCondition" : LoftEndDerivativeType.NORMAL_TO_PROFILE, "startMagnitude" : 1, "endCondition" : LoftEndDerivativeType.NORMAL_TO_PROFILE, "endMagnitude" : 1, "sheetProfilesArray" : [{ "sheetProfileEntities" : qUnion([Q1]) }, { "sheetProfileEntities" : qUnion([Q2]) }]});
        }
    });
